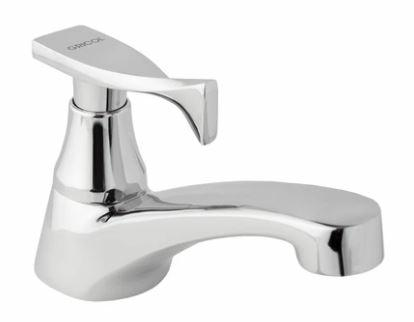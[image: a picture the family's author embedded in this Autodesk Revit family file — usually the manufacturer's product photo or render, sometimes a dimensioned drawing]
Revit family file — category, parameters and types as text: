
# Revit family: 01-28152-11 LLAVE INDIVIDUAL LAVAMANOS METAL PRISTINA
name_source: partatom
category: Plumbing Fixtures
revit_build: Autodesk Revit 2018 (Build: 20170223_1515(x64)
units: mm (PartAtom-declared; Revit-internal decimal feet)

## family parameters
Cut with Voids When Loaded = No
Host = Face
OmniClass Number = 23.31.11.00
Part Type = Normal
Room Calculation Point = No
Round Connector Dimension = Use Diameter
Shared = No

## types (1)
- 01-28152-11
    Alto = 77.9 mm
    Ancho = 137.74 mm  [stored 0.451903 ft]
    CW Connection = Yes
    Default Elevation = 0 mm  [stored 0 ft]
    Description = Llave individual
    Dim base = 46 mm
    Eje - Aireador = 105 mm  [stored 0.344488 ft]
    HW Connection = Yes
    Link Ficha Tecnica = http://infotecnica.gricol.com
    Manija = 75.5 mm  [stored 0.247703 ft]
    Manufacturer = Gricol
    Metal Laton Cromado = Metal Laton Cromado
    Metal Zamak Cromado = Metal Zamak Cromado
    Model = 01-28152-11
    Plastico ABS Cromado = Plastico - ABS Cromado
    Product Name = LLAVE INDIVIDUAL LAVAMANOS METAL PRISTINA
    Type Image = LLAVE INDIVIDUAL LAVAMANOS METAL PRISTINA.JPG
    URL = https://www.gricol.com
    Vent Connection = No
    Waste Connection = No

note: [stored X ft] marks values corroborated as IEEE doubles in the binary element streams (Revit-internal decimal feet)

## geometry (parser evidence)
native form markers: Blend x2, Sweep x4
no freeform markers — native parametric forms only
